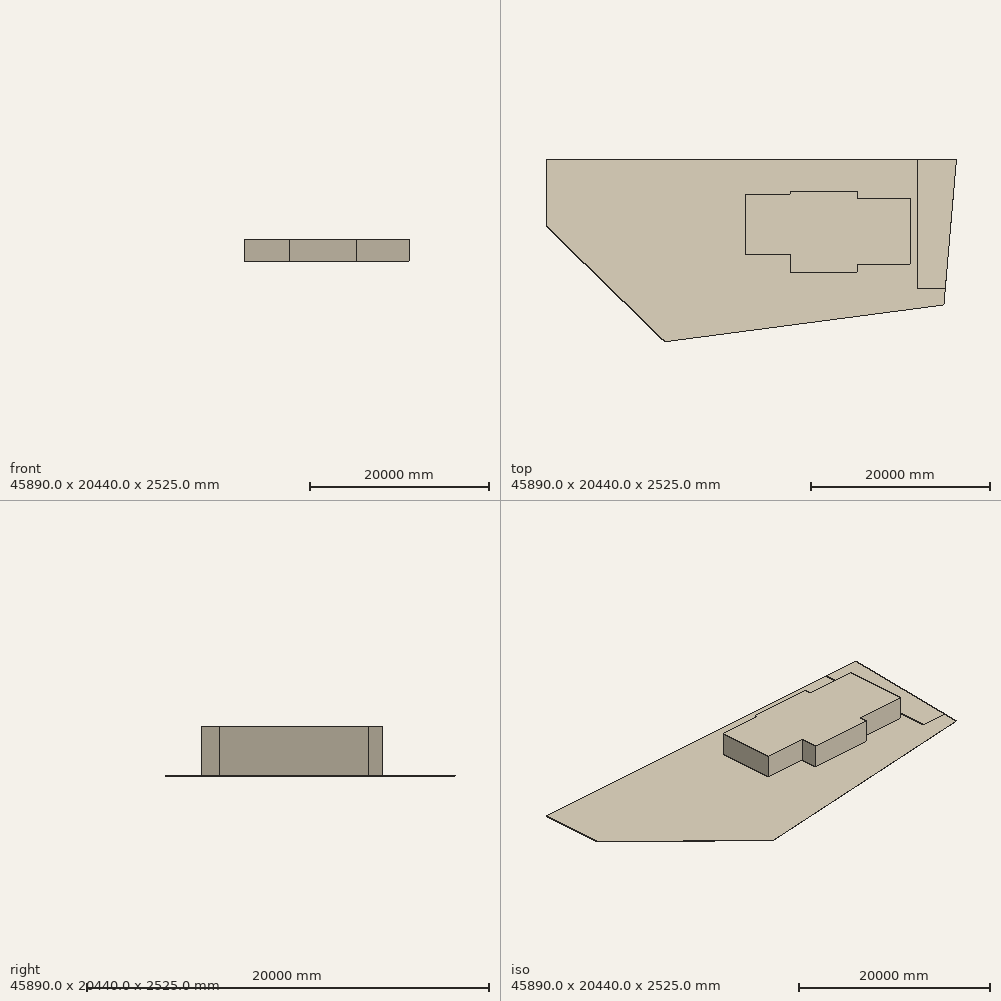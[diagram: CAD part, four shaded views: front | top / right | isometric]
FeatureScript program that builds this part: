
annotation { "Feature Type Name" : "Feature", "Feature Type Description" : "" }
export const myFeature = defineFeature(function(context is Context, id is Id, definition is map)
    precondition{}
    {
        {
            var Q0;
            Q0=qCreatedBy(makeId("Top.planeOp"),FACE);
            var sketch = newSketch(context, id + "F0", { "sketchPlane" : qUnion([Q0])});
            skLineSegment(sketch, "E0.bottom", {"start": v(-1081.12, 4915.65) * mm, "end": v(4918.88, 4915.65) * mm});
            skLineSegment(sketch, "E0.top", {"start": v(-1081.12, -2484.35) * mm, "end": v(4918.88, -2484.35) * mm});
            skLineSegment(sketch, "E0.right", {"start": v(4918.88, 4915.65) * mm, "end": v(4918.88, -2484.35) * mm});
            skLineSegment(sketch, "E1", {"start": v(-1081.12, 4915.65) * mm, "end": v(-1081.12, 5615.65) * mm});
            skLineSegment(sketch, "E2", {"start": v(-1081.12, 5615.65) * mm, "end": v(-8581.12, 5615.65) * mm});
            skLineSegment(sketch, "E3", {"start": v(-8581.12, 5615.65) * mm, "end": v(-8581.12, 5365.65) * mm});
            skLineSegment(sketch, "E4", {"start": v(-8581.12, -3384.35) * mm, "end": v(-1081.12, -3384.35) * mm});
            skLineSegment(sketch, "E5", {"start": v(-1081.12, -3384.35) * mm, "end": v(-1081.12, -2484.35) * mm});
            skLineSegment(sketch, "E6", {"start": v(-8581.12, 5365.65) * mm, "end": v(-13581.12, 5365.65) * mm});
            skLineSegment(sketch, "E7", {"start": v(-13581.12, 5365.65) * mm, "end": v(-13581.12, -1384.35) * mm});
            skLineSegment(sketch, "E8", {"start": v(-13581.12, -1384.35) * mm, "end": v(-8581.12, -1384.35) * mm});
            skLineSegment(sketch, "E9.trimOffspring", {"start": v(-8581.12, -1384.35) * mm, "end": v(-8581.12, -3384.35) * mm});
            skSolve(sketch);
        }
        {
            var Q0;
            Q0=makeQuery(id+"F0.imprint","IMPRINT",FACE,{"disambiguationData":[TD([[makeQuery(id+"F0.imprint","IMPRINT",EDGE,{"derivedFrom":sQuery(id+"F0.wireOp",EDGE,"E0.bottom")}),-1.0]])]});
            extrude(context, id + "F1", {"entities" : qUnion([Q0]), "depth" : 2500 * mm, "offsetDistance" : 25 * mm});
        }
        {
            var Q0;
            Q0=qCreatedBy(makeId("Top.planeOp"),FACE);
            var sketch = newSketch(context, id + "F2", { "sketchPlane" : qUnion([Q0])});
            skLineSegment(sketch, "E10.0", {"start": v(10038.88, 9275.65) * mm, "end": v(-35851.12, 9275.65) * mm});
            skLineSegment(sketch, "E11", {"start": v(10038.88, 9275.65) * mm, "end": v(8628.88, -7044.35) * mm});
            skLineSegment(sketch, "E12", {"start": v(8628.88, -7044.35) * mm, "end": v(-22600.52, -11164.35) * mm});
            skLineSegment(sketch, "E13", {"start": v(-35851.12, 9275.65) * mm, "end": v(-35851.12, 1745.79) * mm});
            skLineSegment(sketch, "E14", {"start": v(-35851.12, 1745.79) * mm, "end": v(-22600.52, -11164.35) * mm});
            skSolve(sketch);
        }
        {
            var Q0;
            Q0 = qSketchRegion(id + "F2", true);
            extrude(context, id + "F3", {"entities" : qUnion([Q0]), "oppositeDirection" : true, "depth" : 25 * mm, "offsetDistance" : 25 * mm});
        }
        {
            var Q0;
            Q0=makeQuery(id+"F3.opExtrude","CAP_FACE",FACE,{"disambiguationData":[OSD([sQuery(id+"F2.wireOp",EDGE,"E10.0"),sQuery(id+"F2.wireOp",EDGE,"E11"),sQuery(id+"F2.wireOp",EDGE,"E12"),sQuery(id+"F2.wireOp",EDGE,"E13"),sQuery(id+"F2.wireOp",EDGE,"E14")])],"isStart":true});
            var sketch = newSketch(context, id + "F4", { "sketchPlane" : qUnion([Q0])});
            skLineSegment(sketch, "E15.0", {"start": v(5638.88, 9275.65) * mm, "end": v(5638.88, -5163.1) * mm});
            skLineSegment(sketch, "E16", {"start": v(8789.58, -5184.4) * mm, "end": v(5638.88, -5163.1) * mm});
            skPoint(sketch, "E17.orphan", {"position": v(-35851.12, 9275.65) * mm});
            skPoint(sketch, "E18.orphan", {"position": v(10038.88, 9275.65) * mm});
            skSolve(sketch);
        }
        {
            var Q0;
            {var subQ0=sQuery(id+"F4.wireOp",EDGE,"E15.0");Q0=makeQuery(id+"F4.imprint","IMPRINT",FACE,{"disambiguationData":[TD([[makeQuery(id+"F4.imprint","IMPRINT",EDGE,{"derivedFrom":subQ0}),1.0]])]});}
            extrude(context, id + "F5", {"entities" : qUnion([Q0]), "depth" : 25 * mm, "offsetDistance" : 25 * mm});
        }
    });
